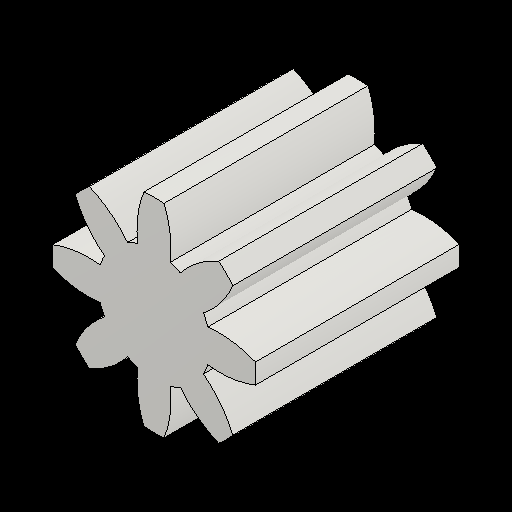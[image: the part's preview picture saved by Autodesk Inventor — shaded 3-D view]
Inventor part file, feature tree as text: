
AUTODESK INVENTOR PART (.ipt)
format: ipt  version: 2023.2 (Build 272271030, 271C)  size: 177,152 bytes
history: native  units: mm (DEFAULTED — no unit token found)
features: plane x3, other x3, sketch x2, extrude x1
ambient origin geometry x8: Origin, YZ Plane, XZ Plane, XY Plane, X Axis, Y Axis, Z Axis, Center Point
bodies: Solid1 (feature_tree)
feature tree (9):
  extrude  "Extrusion1"  Depth=10.0mm TaperAngle=0.0deg
  plane  "Work Plane2"
  plane  "Work Plane8"
  plane  "Work Plane9"
  other  "Spur Gear"
  sketch  "Sketch1"  dims[d0=10.0mm d1=10.0mm d2=0.0mm]
  sketch  "Sketch2"  dims[d3=8.0mm d4=10.0mm d5=0.0mm d16=16.5mm d17=0.0mm d34=22.5deg d39=0.0mm d41=0.0mm d43=16.5mm d46=16.5mm d47=0.0mm d48=0.0mm]
  other  "Srf1"
  other  "Pitch Diameter"
